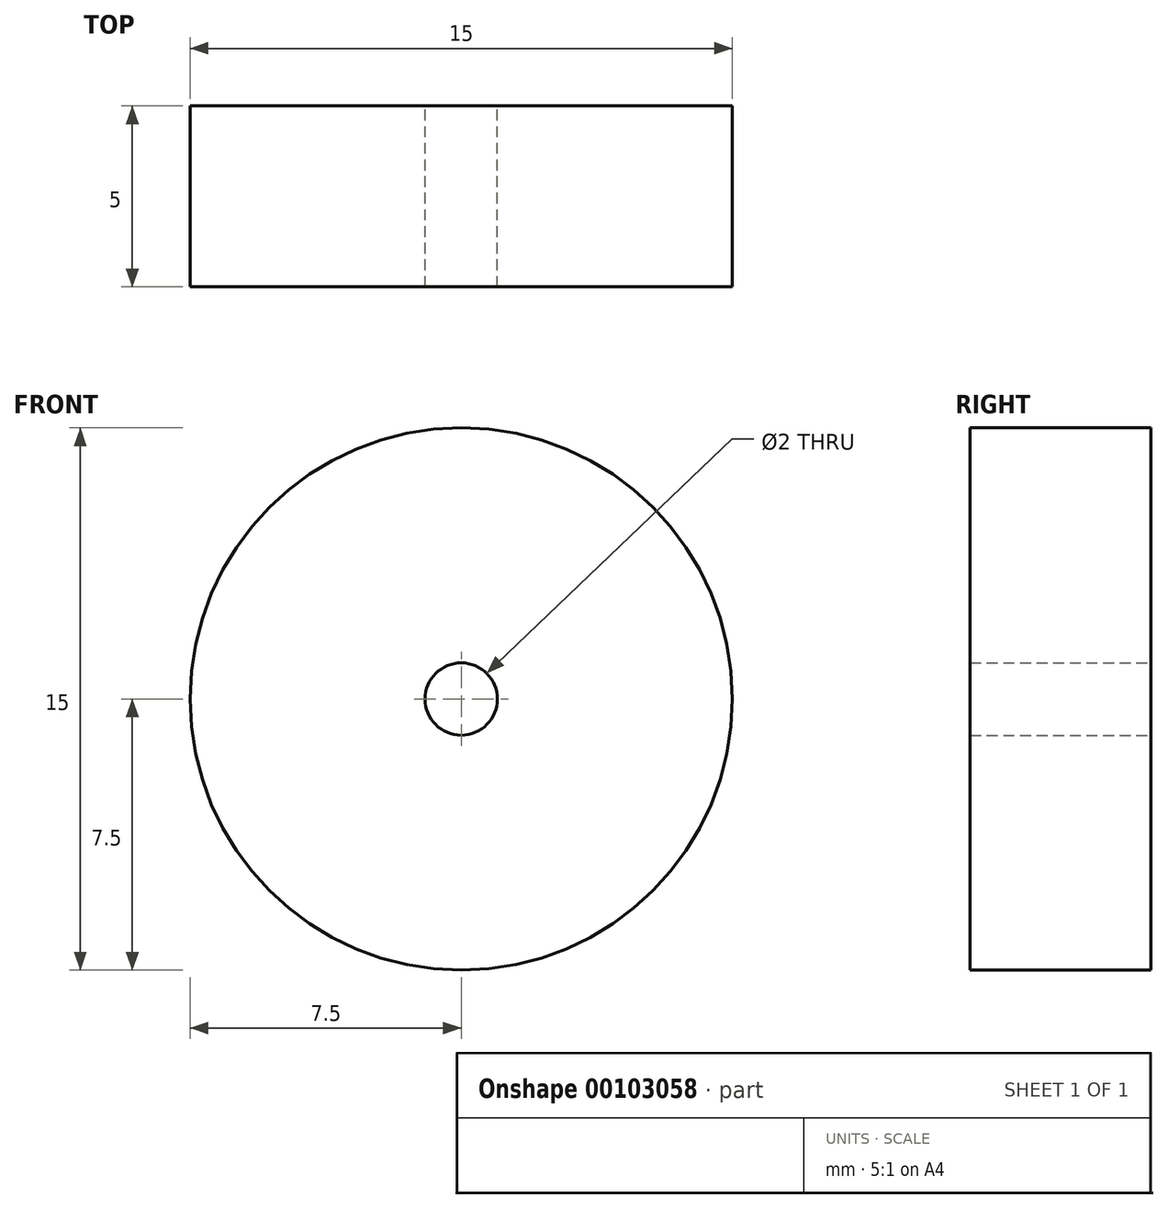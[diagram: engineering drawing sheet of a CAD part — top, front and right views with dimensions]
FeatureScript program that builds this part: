
annotation { "Feature Type Name" : "Feature", "Feature Type Description" : "" }
export const myFeature = defineFeature(function(context is Context, id is Id, definition is map)
    precondition{}
    {
        {
            var Q0;
            Q0=qCreatedBy(makeId("Front.planeOp"),FACE);
            var sketch = newSketch(context, id + "F0", { "sketchPlane" : qUnion([Q0])});
            skCircle(sketch, "E0", {"center": v(0, 0) * mm, "radius": 7.5 * mm});
            skCircle(sketch, "E1", {"center": v(0, 0) * mm, "radius": 1 * mm});
            skSolve(sketch);
        }
        {
            var Q0;
            Q0=makeQuery(id+"F0.imprint","IMPRINT",FACE,{"disambiguationData":[TD([[makeQuery(id+"F0.imprint","IMPRINT",EDGE,{"derivedFrom":sQuery(id+"F0.wireOp",EDGE,"E0")}),1.0]])]});
            extrude(context, id + "F1", {"entities" : qUnion([Q0]), "endBound" : BoundingType.SYMMETRIC, "depth" : 5 * mm});
        }
    });
